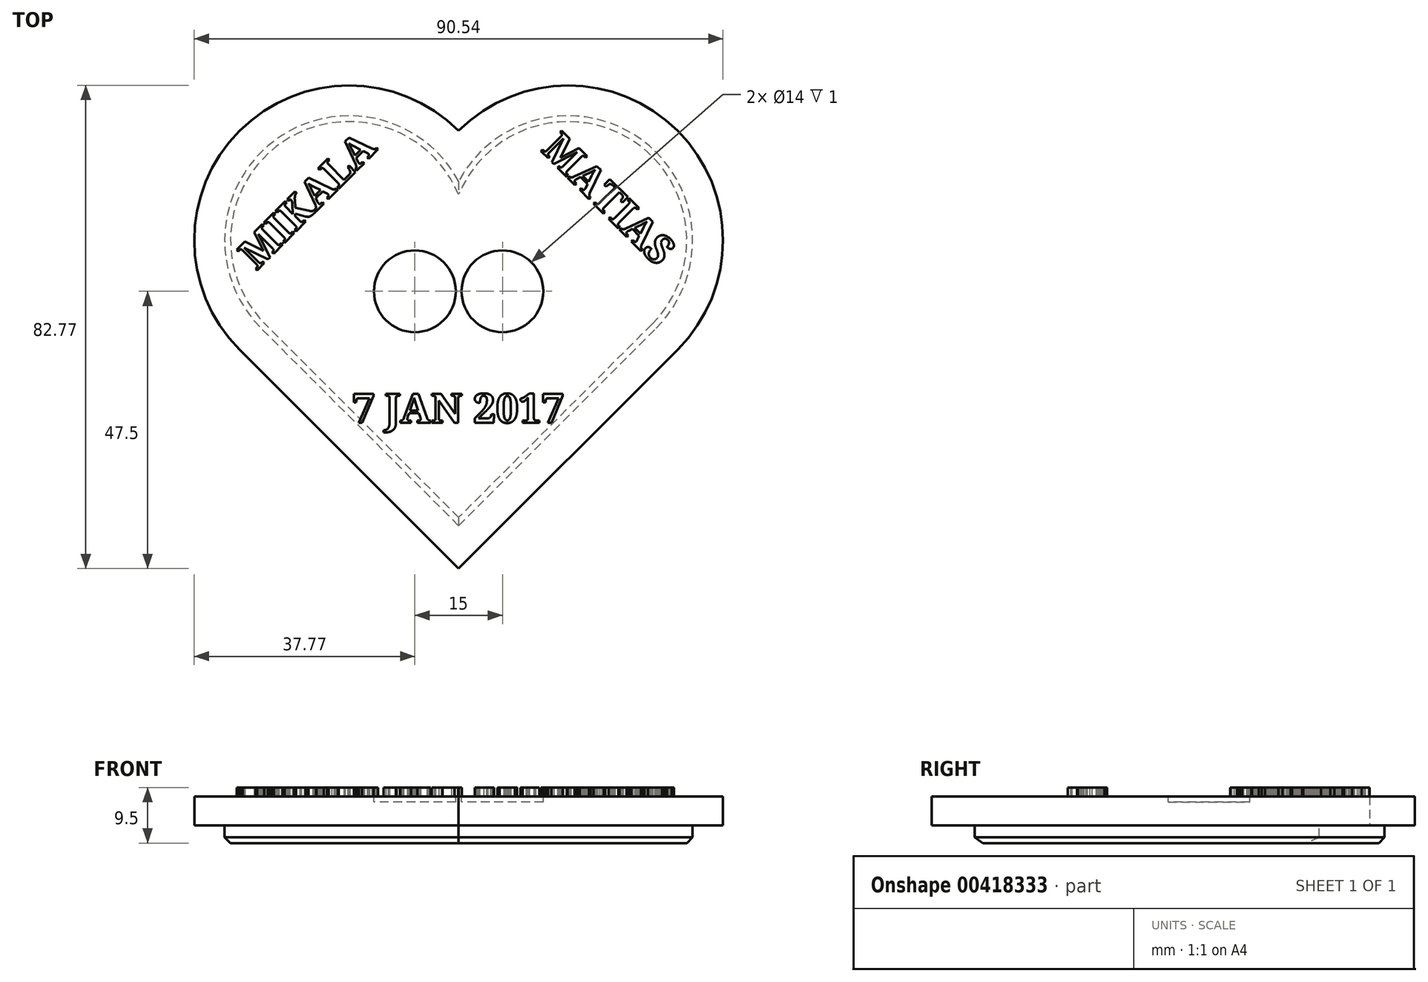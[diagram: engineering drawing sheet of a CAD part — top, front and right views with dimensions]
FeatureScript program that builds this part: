
annotation { "Feature Type Name" : "Feature", "Feature Type Description" : "" }
export const myFeature = defineFeature(function(context is Context, id is Id, definition is map)
    precondition{}
    {
        {
            var Q0;
            Q0=qCreatedBy(makeId("Top.planeOp"),FACE);
            var sketch = newSketch(context, id + "F0", { "sketchPlane" : qUnion([Q0])});
            skLineSegment(sketch, "E0", {"start": v(0, 0) * mm, "end": v(-37.5, 37.5) * mm});
            skLineSegment(sketch, "E1", {"start": v(0, 0) * mm, "end": v(37.5, 37.5) * mm});
            skArc(sketch, "E2", {"start": v(37.5, 37.5) * mm, "mid": v(37.5, 75) * mm, "end": v(0, 75) * mm});
            skArc(sketch, "E3", {"start": v(0, 75) * mm, "mid": v(-37.5, 75) * mm, "end": v(-37.5, 37.5) * mm});
            skLineSegment(sketch, "E4.0", {"start": v(0, 7.35) * mm, "end": v(-33.82, 41.18) * mm});
            skLineSegment(sketch, "E4.1", {"start": v(0, 7.35) * mm, "end": v(33.82, 41.18) * mm});
            skArc(sketch, "E4.2", {"start": v(33.82, 41.18) * mm, "mid": v(31.5, 73.34) * mm, "end": v(0, 66.4) * mm});
            skArc(sketch, "E4.3", {"start": v(0, 66.4) * mm, "mid": v(-31.5, 73.34) * mm, "end": v(-33.82, 41.18) * mm});
            skLineSegment(sketch, "E5", {"start": v(37.5, 37.5) * mm, "end": v(0, 75) * mm, "construction": true});
            skLineSegment(sketch, "E6", {"start": v(0, 75) * mm, "end": v(-37.5, 37.5) * mm, "construction": true});
            skSolve(sketch);
        }
        {
            var Q0;
            Q0=makeQuery(id+"F0.imprint","IMPRINT",FACE,{"disambiguationData":[TD([[makeQuery(id+"F0.imprint","IMPRINT",EDGE,{"derivedFrom":sQuery(id+"F0.wireOp",EDGE,"E0")}),-1.0]])]});
            var Q1;
            Q1=makeQuery(id+"F0.imprint","IMPRINT",FACE,{"disambiguationData":[TD([[makeQuery(id+"F0.imprint","IMPRINT",EDGE,{"derivedFrom":sQuery(id+"F0.wireOp",EDGE,"E4.0")}),-1.0]])]});
            extrude(context, id + "F1", {"entities" : qUnion([Q0, Q1]), "depth" : 5 * mm});
        }
        {
            var Q0;
            Q0=makeQuery(id+"F0.imprint","IMPRINT",FACE,{"disambiguationData":[TD([[makeQuery(id+"F0.imprint","IMPRINT",EDGE,{"derivedFrom":sQuery(id+"F0.wireOp",EDGE,"E4.0")}),-1.0]])]});
            extrude(context, id + "F2", {"entities" : qUnion([Q0]), "operationType" : NewBodyOperationType.ADD, "oppositeDirection" : true, "depth" : 3 * mm});
        }
        {
            var Q0;
            Q0=makeQuery(id+"F2.opExtrude","CAP_EDGE",EDGE,{"disambiguationData":[OSD([sQuery(id+"F0.wireOp",EDGE,"E4.3")])],"isStart":false});
            var Q1;
            Q1=makeQuery(id+"F2.opExtrude","CAP_EDGE",EDGE,{"disambiguationData":[OSD([sQuery(id+"F0.wireOp",EDGE,"E4.1")])],"isStart":false});
            chamfer(context, id + "F3", {"entities" : qUnion([Q0, Q1]), "width" : 1 * mm, "tangentPropagation" : true});
        }
        {
            var Q0;
            Q0=makeQuery(id+"F1.opExtrude","CAP_FACE",FACE,{"disambiguationData":[OSD([sQuery(id+"F0.wireOp",EDGE,"E0"),sQuery(id+"F0.wireOp",EDGE,"E1"),sQuery(id+"F0.wireOp",EDGE,"E2"),sQuery(id+"F0.wireOp",EDGE,"E3")])],"isStart":false});
            var sketch = newSketch(context, id + "F4", { "sketchPlane" : qUnion([Q0])});
            skLineSegment(sketch, "E7", {"start": v(-37.5, 37.5) * mm, "end": v(37.5, 37.5) * mm, "construction": true});
            skCircle(sketch, "E8", {"center": v(-7.5, 47.5) * mm, "radius": 7 * mm});
            skCircle(sketch, "E9", {"center": v(7.5, 47.5) * mm, "radius": 7 * mm});
            skSolve(sketch);
        }
        {
            var Q0;
            Q0=makeQuery(id+"F4.imprint","IMPRINT",FACE,{"disambiguationData":[TD([[makeQuery(id+"F4.imprint","IMPRINT",EDGE,{"derivedFrom":sQuery(id+"F4.wireOp",EDGE,"E8")}),1.0]])]});
            var Q1;
            Q1=makeQuery(id+"F4.imprint","IMPRINT",FACE,{"disambiguationData":[TD([[makeQuery(id+"F4.imprint","IMPRINT",EDGE,{"derivedFrom":sQuery(id+"F4.wireOp",EDGE,"E9")}),1.0]])]});
            extrude(context, id + "F5", {"entities" : qUnion([Q0, Q1]), "operationType" : NewBodyOperationType.REMOVE, "oppositeDirection" : true, "depth" : 1 * mm});
        }
        {
            var Q0;
            Q0=makeQuery(id+"F1.opExtrude","CAP_FACE",FACE,{"disambiguationData":[OSD([sQuery(id+"F0.wireOp",EDGE,"E0"),sQuery(id+"F0.wireOp",EDGE,"E1"),sQuery(id+"F0.wireOp",EDGE,"E2"),sQuery(id+"F0.wireOp",EDGE,"E3")])],"isStart":false});
            var sketch = newSketch(context, id + "F6", { "sketchPlane" : qUnion([Q0])});
            skText(sketch, "E10", { "text": "MIKALA", "fontName": "NotoSerif-Bold.ttf"});
            skText(sketch, "E11", { "text": "MATIAS", "fontName": "NotoSerif-Bold.ttf"});
            skText(sketch, "E12", { "text": "7 JAN 2017", "fontName": "NotoSerif-Bold.ttf"});
            const initialGuessF6  = {"E10": [-0.03464, 0.05097, 0.7071, 0.7071, 0.005], "E11": [0.01396, 0.07165, 0.7071, -0.7071, 0.005], "E12": [-0.01825, 0.025, 1, 0, 0.005]};
            skSetInitialGuess(sketch, initialGuessF6);
            skSolve(sketch);
        }
        {
            var Q0;
            Q0 = qSketchRegion(id + "F6", true);
            extrude(context, id + "F7", {"entities" : qUnion([Q0]), "operationType" : NewBodyOperationType.ADD, "depth" : 1.5 * mm});
        }
    });
